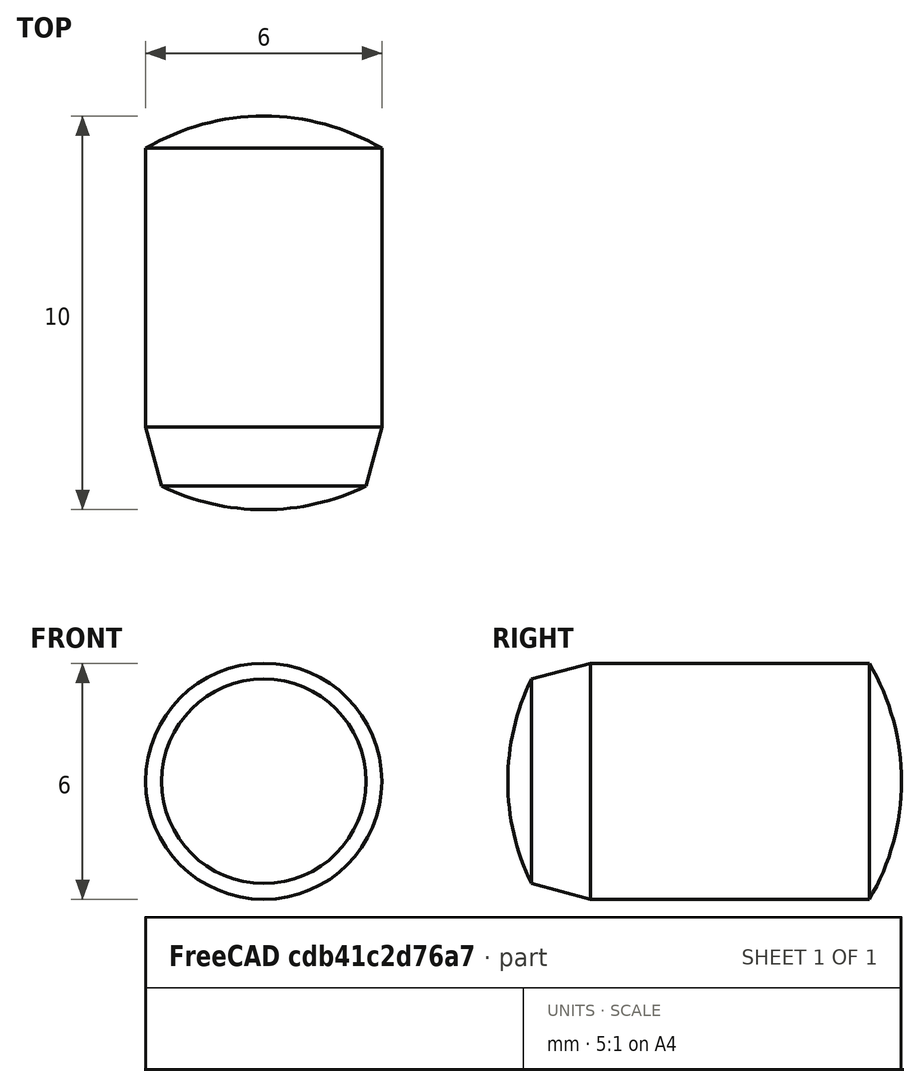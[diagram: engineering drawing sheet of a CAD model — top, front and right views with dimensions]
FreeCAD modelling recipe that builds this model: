
FCSTD DOCUMENT  (FreeCAD 0.15R4470 (Git))
Label: Zyl-Stift_DIN_6325-6x10
License: CC-BY 3.0
LicenseURL: http://creativecommons.org/licenses/by/3.0/
objects: Sketcher::SketchObject×1, PartDesign::Revolution×1
note: 3 computed .brp shape members not serialized (recipe doc carries the construction recipe); baked Part::Feature solids carry a one-line shape summary decoded from their .brp

FEATURE [Sketcher::SketchObject] Sketch
  Placement = pos=(0,0,0) rot=(0.57735,0.57735,0.57735;2.0944rad)
  sketch-geometry (5):
    g0: ArcOfCircle CenterX=5.325 CenterY=0 CenterZ=0 NormalX=0 NormalY=0 NormalZ=1 Radius=5.925 StartAngle=2.68767 EndAngle=3.14159
    g1: LineSegment StartX=0 StartY=2.59808 StartZ=0 EndX=1.5 EndY=3 EndZ=0
    g2: LineSegment StartX=1.5 StartY=3 StartZ=0 EndX=8.58437 EndY=3 EndZ=0
    g3: ArcOfCircle CenterX=3.475 CenterY=0 CenterZ=0 NormalX=0 NormalY=0 NormalZ=1 Radius=5.925 StartAngle=0 EndAngle=0.530923
    g4: LineSegment StartX=-0.6 StartY=0 StartZ=0 EndX=9.4 EndY=0 EndZ=0
  constraints (17):
    c: PointOnObject(g0,g-1)
    c: PointOnObject(g0,g-1)
    c: PointOnObject(g0,g-2)
    c: Coincident(g0,g1)
    c: Coincident(g1,g2)
    c: Horizontal(g2)
    c: PointOnObject(g3,g-1)
    c: Coincident(g3,g2)
    c: PointOnObject(g3,g-1)
    c: Coincident(g4,g0)
    c: Coincident(g4,g3)
    c: Equal(g0,g3)
    c: Angle(g4,g1) = 0.261799
    c: DistanceX(g4) = 10
    c: DistanceY(g-1,g1) = 3
    c: DistanceX(g1) = 1.5
    c: DistanceX(g0,g0) = 0.6
FEATURE [PartDesign::Revolution] Revolution  label="Zyl-Stift DIN 6325-6x10 #"
  Angle = 360
  Axis = (0,1,0)
  Base = (0,0,0)
  Placement = pos=(0,0,0) rot=(0.57735,0.57735,0.57735;2.0944rad)
  ReferenceAxis = -> Sketch [H_Axis]
  Sketch = -> Sketch
